AUTODESK INVENTOR PART (.ipt)
format: ipt  version: 2018 (Build 220112000, 112)  size: 118,784 bytes
history: native  units: in
note: dims shown in document units (in); Inventor stores cm internally (conversion verified against a paired STEP export)
features: sketch x1
ambient origin geometry x8: Origin, YZ Plane, XZ Plane, XY Plane, X Axis, Y Axis, Z Axis, Center Point
feature tree (1):
  sketch  "Sketch1"  dims[d0=0.2047in d1=0.2047in d2=0.2047in d3=0.2047in d4=0.2047in d5=0.2047in d6=0.1614in d7=0.1614in d8=0.1614in d9=0.1614in d10=0.125in d11=0.125in d12=0.125in d13=0.125in d14=0.125in d15=0.125in d16=0.125in d17=0.125in d18=0.1614in d19=0.1614in d20=0.1614in]
